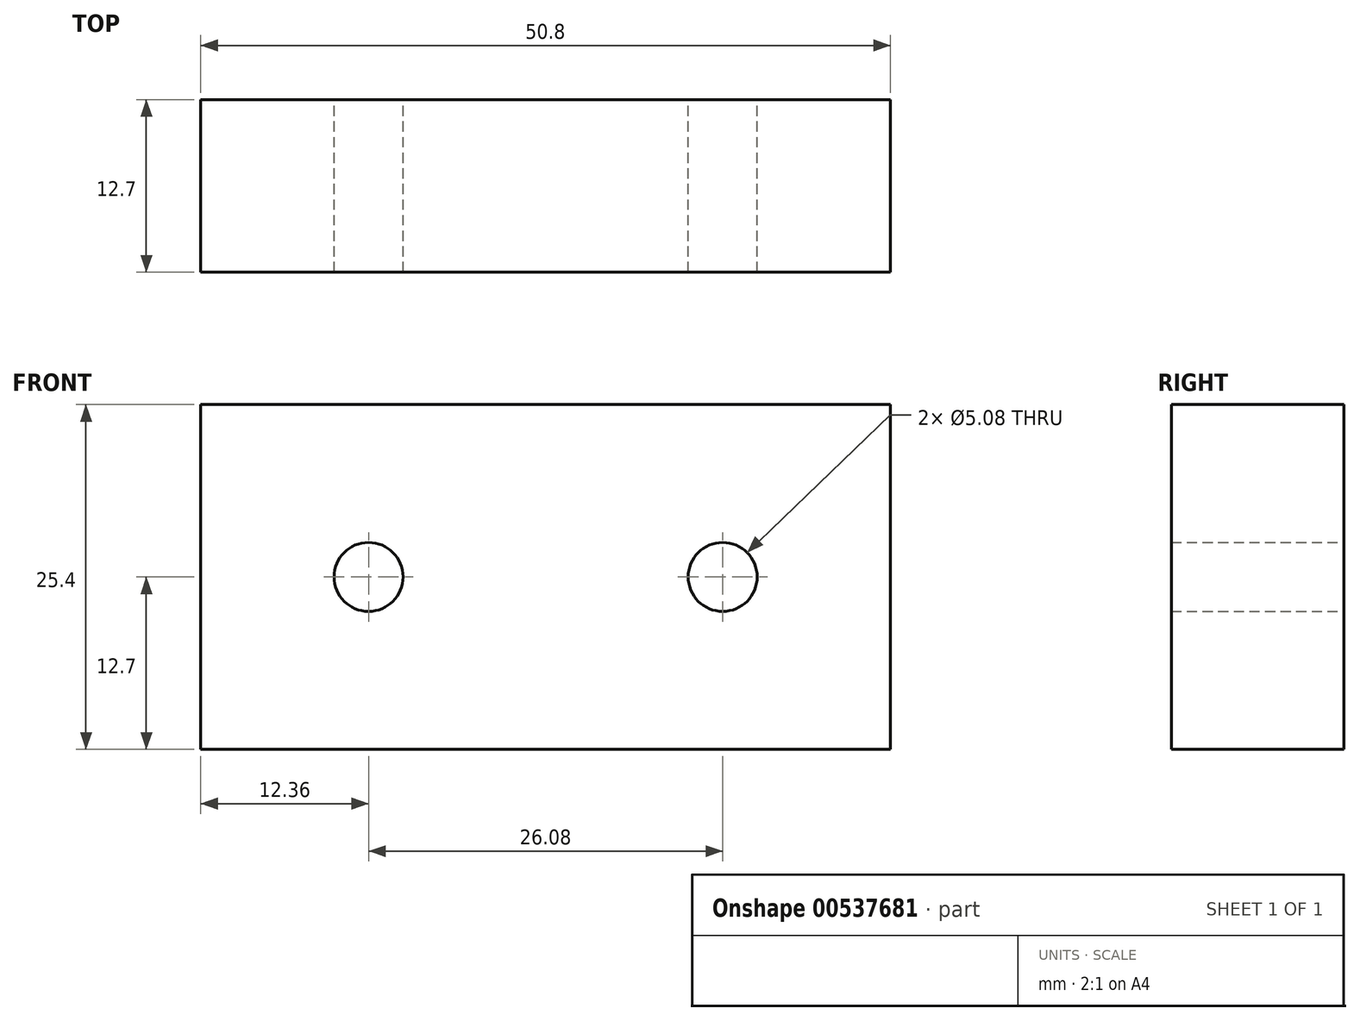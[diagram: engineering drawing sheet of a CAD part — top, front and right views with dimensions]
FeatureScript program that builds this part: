
annotation { "Feature Type Name" : "Feature", "Feature Type Description" : "" }
export const myFeature = defineFeature(function(context is Context, id is Id, definition is map)
    precondition{}
    {
        {
            var Q0;
            Q0=qCreatedBy(makeId("Front.planeOp"),FACE);
            var sketch = newSketch(context, id + "F0", { "sketchPlane" : qUnion([Q0])});
            skLineSegment(sketch, "E0.bottom", {"start": v(-25.4, 12.7) * mm, "end": v(25.4, 12.7) * mm});
            skLineSegment(sketch, "E0.top", {"start": v(-25.4, -12.7) * mm, "end": v(25.4, -12.7) * mm});
            skLineSegment(sketch, "E0.left", {"start": v(-25.4, 12.7) * mm, "end": v(-25.4, -12.7) * mm});
            skLineSegment(sketch, "E0.right", {"start": v(25.4, 12.7) * mm, "end": v(25.4, -12.7) * mm});
            skPoint(sketch, "E0.middle", {"position": v(0, 0) * mm});
            skCircle(sketch, "E1", {"center": v(-13.04, 0) * mm, "radius": 2.54 * mm});
            skCircle(sketch, "E2.MirrorC", {"center": v(13.04, 0) * mm, "radius": 2.54 * mm});
            skSolve(sketch);
        }
        {
            var Q0;
            Q0=makeQuery(id+"F0.imprint","IMPRINT",FACE,{"disambiguationData":[TD([[makeQuery(id+"F0.imprint","IMPRINT",EDGE,{"derivedFrom":sQuery(id+"F0.wireOp",EDGE,"E0.bottom")}),-1.0]])]});
            extrude(context, id + "F1", {"entities" : qUnion([Q0]), "depth" : 12.7 * mm, "offsetDistance" : 25.4 * mm});
        }
    });
